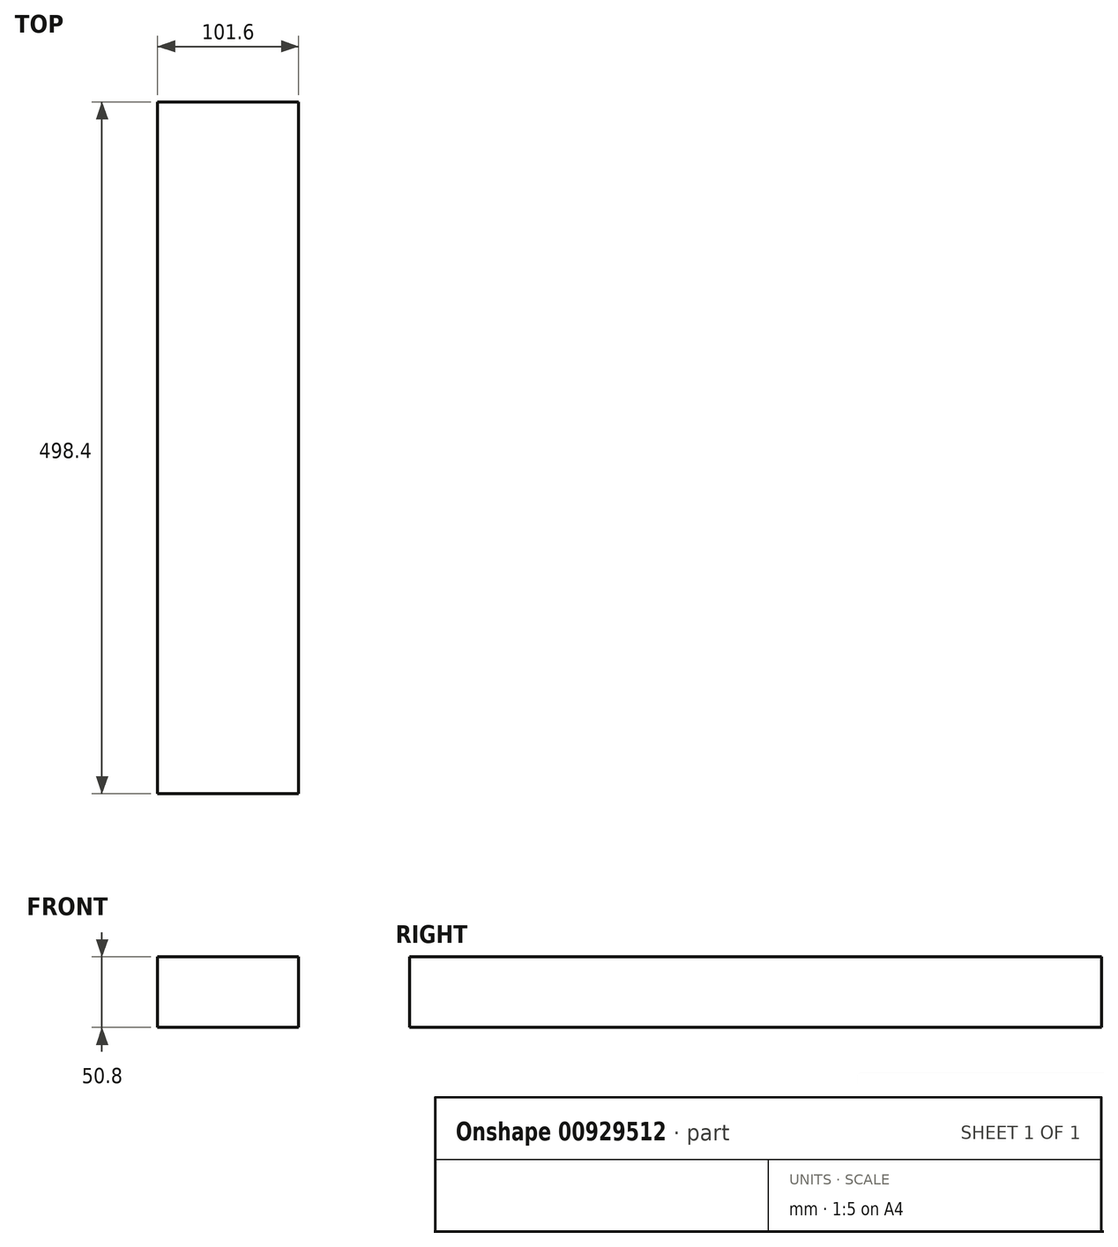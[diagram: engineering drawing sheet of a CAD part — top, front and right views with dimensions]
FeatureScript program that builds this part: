
annotation { "Feature Type Name" : "Feature", "Feature Type Description" : "" }
export const myFeature = defineFeature(function(context is Context, id is Id, definition is map)
    precondition{}
    {
        {
            var Q0;
            Q0=qCreatedBy(makeId("Front.planeOp"),FACE);
            var sketch = newSketch(context, id + "F0", { "sketchPlane" : qUnion([Q0])});
            skLineSegment(sketch, "E0", {"start": v(0, 0) * mm, "end": v(50.8, 0) * mm});
            skLineSegment(sketch, "E1", {"start": v(0, 0) * mm, "end": v(-50.8, 0) * mm});
            skLineSegment(sketch, "E2", {"start": v(50.8, 0) * mm, "end": v(50.8, 50.8) * mm});
            skLineSegment(sketch, "E3", {"start": v(-50.8, 0) * mm, "end": v(-50.8, 50.8) * mm});
            skLineSegment(sketch, "E4", {"start": v(-50.8, 50.8) * mm, "end": v(50.8, 50.8) * mm});
            skSolve(sketch);
        }
        {
            var Q0;
            Q0=makeQuery(id+"F0.imprint","IMPRINT",FACE,{"disambiguationData":[TD([[makeQuery(id+"F0.imprint","IMPRINT",EDGE,{"derivedFrom":sQuery(id+"F0.wireOp",EDGE,"E0")}),1.0]])]});
            extrude(context, id + "F1", {"entities" : qUnion([Q0]), "depth" : 498.4 * mm, "offsetDistance" : 25 * mm});
        }
    });
